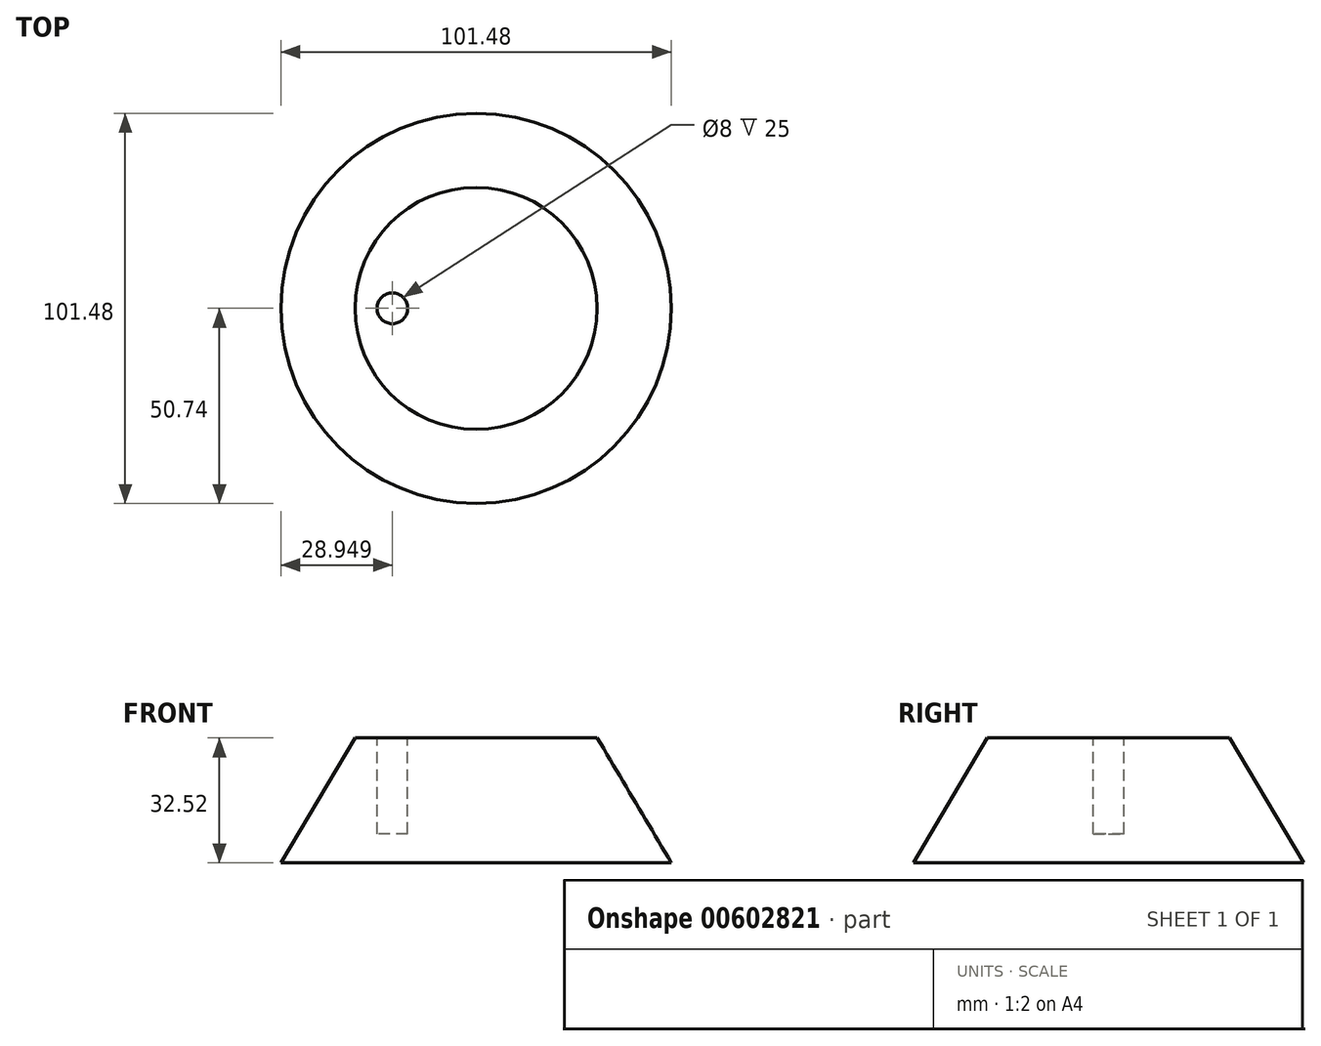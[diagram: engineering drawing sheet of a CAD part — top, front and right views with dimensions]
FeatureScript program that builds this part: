
annotation { "Feature Type Name" : "Feature", "Feature Type Description" : "" }
export const myFeature = defineFeature(function(context is Context, id is Id, definition is map)
    precondition{}
    {
        {
            var Q0;
            Q0=qCreatedBy(makeId("Front.planeOp"),FACE);
            var sketch = newSketch(context, id + "F0", { "sketchPlane" : qUnion([Q0])});
            skLineSegment(sketch, "E0", {"start": v(0, 0) * mm, "end": v(50.74, 0) * mm});
            skLineSegment(sketch, "E1", {"start": v(50.74, 0) * mm, "end": v(31.47, 32.52) * mm});
            skLineSegment(sketch, "E2", {"start": v(31.47, 32.52) * mm, "end": v(0, 32.52) * mm});
            skLineSegment(sketch, "E3", {"start": v(0, 32.52) * mm, "end": v(0, 0) * mm});
            skSolve(sketch);
        }
        {
            var Q0;
            Q0 = qSketchRegion(id + "F0", true);
            var Q1;
            Q1=sQuery(id+"F0.wireOp",EDGE,"E3");
            revolve(context, id + "F1", {"entities" : qUnion([Q0]), "axis" : qUnion([Q1]), "revolveType" : RevolveType.FULL});
        }
        {
            var Q0;
            Q0=makeQuery(id+"F1.opRevolve","SWEPT_FACE",FACE,{"disambiguationData":[OSD([sQuery(id+"F0.wireOp",EDGE,"E2")])]});
            var sketch = newSketch(context, id + "F2", { "sketchPlane" : qUnion([Q0])});
            skCircle(sketch, "E4", {"center": v(-21.8, 0) * mm, "radius": 4 * mm});
            skSolve(sketch);
        }
        {
            var Q0;
            Q0=makeQuery(id+"F2.imprint","IMPRINT",FACE,{"disambiguationData":[TD([[makeQuery(id+"F2.imprint","IMPRINT",EDGE,{"derivedFrom":sQuery(id+"F2.wireOp",EDGE,"E4")}),1.0]])]});
            var Q1;
            Q1=sQuery(id+"F2.wireOp",EDGE,"E4");
            extrude(context, id + "F3", {"entities" : qUnion([Q0]), "operationType" : NewBodyOperationType.REMOVE, "surfaceEntities" : qUnion([Q1]), "oppositeDirection" : true, "depth" : 25 * mm, "offsetDistance" : 25 * mm});
        }
    });
